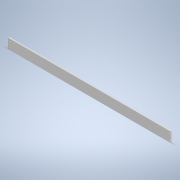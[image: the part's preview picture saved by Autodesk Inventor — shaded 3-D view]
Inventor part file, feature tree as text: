
AUTODESK INVENTOR PART (.ipt)
format: ipt  version: 2020 (Build 240168000, 168)  size: 127,488 bytes
history: native  units: in
note: dims shown in document units (in); Inventor stores cm internally (conversion verified against a paired STEP export)
features: other x4, extrude x2, sketch x2, reference x2
ambient origin geometry x8: Origin, YZ Plane, XZ Plane, XY Plane, X Axis, Y Axis, Z Axis, Center Point
bodies: Solid1 (feature_tree)
feature tree (10):
  extrude  "Extrusion1"  Depth=0.25in
  extrude  "Extrusion2"  Depth=0.25in
  sketch  "Sketch1"  dims[d0=0.25in d1=0.0in d2=1.0in]
  reference  "Reference1"
  reference  "Reference2"
  sketch  "Sketch2"  dims[d3=0.25in d4=0.25in d5=0.25in d6=0.0in d9=1.0in d10=0.5in]
  other  "<userpath>\Desktop\PnP Machine\PnP Machine.iam"
  other  "PnP Machine.iam"
  other  "YClampTop:2"
  other  "YClampTop:3"
